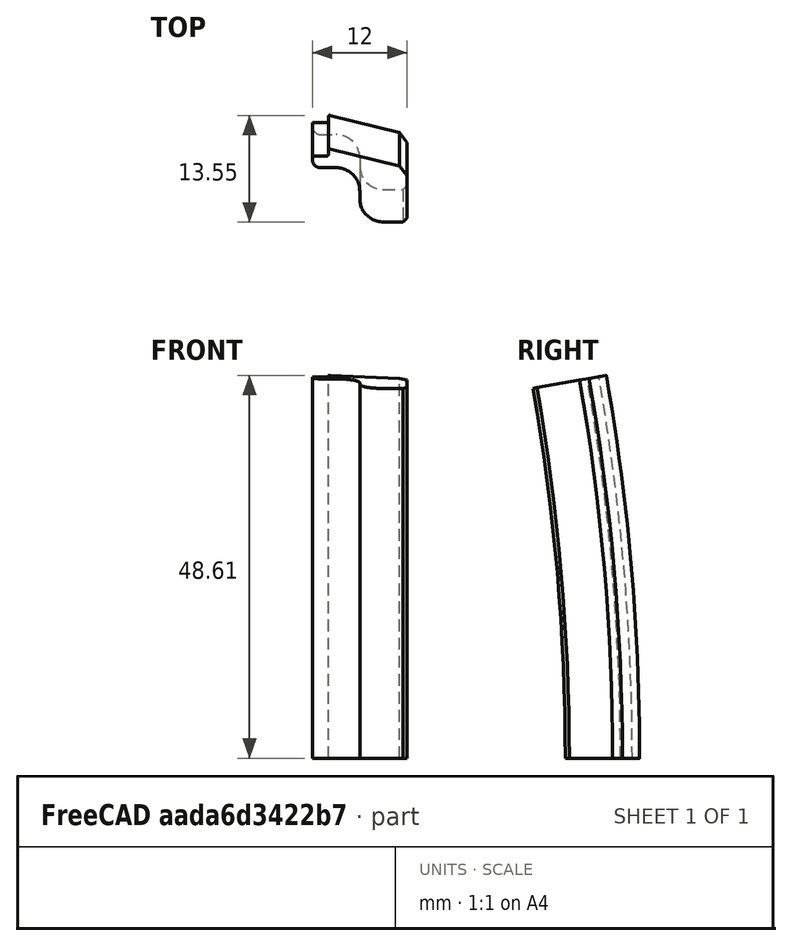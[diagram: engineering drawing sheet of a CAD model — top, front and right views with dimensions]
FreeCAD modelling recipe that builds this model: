
FCSTD DOCUMENT  (FreeCAD 0.16R)
Label: BeadBlock1
License: All rights reserved
LicenseURL: http://en.wikipedia.org/wiki/All_rights_reserved
objects: PartDesign::Fillet×5, PartDesign::Chamfer×2, Sketcher::SketchObject×1, PartDesign::Revolution×1, Mesh::Feature×1
note: 10 computed .brp shape members not serialized (recipe doc carries the construction recipe); baked Part::Feature solids carry a one-line shape summary decoded from their .brp

FEATURE [Sketcher::SketchObject] Sketch
  sketch-geometry (8):
    g0: LineSegment StartX=0 StartY=279 StartZ=0 EndX=2 EndY=279 EndZ=0
    g1: LineSegment StartX=2 StartY=279 StartZ=0 EndX=2 EndY=280 EndZ=0
    g2: LineSegment StartX=0 StartY=277.5 StartZ=0 EndX=0 EndY=279 EndZ=0
    g3: LineSegment StartX=0 StartY=277.5 StartZ=0 EndX=6 EndY=277.5 EndZ=0
    g4: LineSegment StartX=6 StartY=277.5 StartZ=0 EndX=6 EndY=270.5 EndZ=0
    g5: LineSegment StartX=6 StartY=270.5 StartZ=0 EndX=12 EndY=270.5 EndZ=0
    g6: LineSegment StartX=12 StartY=270.5 StartZ=0 EndX=12 EndY=277.5 EndZ=0
    g7: LineSegment StartX=2 StartY=280 StartZ=0 EndX=12 EndY=277.5 EndZ=0
  constraints (24):
    c: Horizontal(g0)
    c: PointOnObject(g0,g-2)
    c: DistanceY(g0) = 279
    c: Distance(g0) = 2
    c: Coincident(g1,g0)
    c: Vertical(g1)
    c: Distance(g1) = 1
    c: Vertical(g2)
    c: Coincident(g2,g0)
    c: Distance(g2) = 1.5
    c: Horizontal(g3)
    c: Coincident(g3,g2)
    c: Distance(g3) = 6
    c: Vertical(g4)
    c: Coincident(g4,g3)
    c: Distance(g4) = 7
    c: Horizontal(g5)
    c: Coincident(g5,g4)
    c: Distance(g5) = 6
    c: Vertical(g6)
    c: Coincident(g5,g6)
    c: Distance(g6) = 7
    c: Coincident(g7,g1)
    c: Coincident(g7,g6)
FEATURE [PartDesign::Revolution] Revolution
  Angle = 10
  Axis = (1,0,0)
  Base = (0,0,0)
  ReferenceAxis = -> Sketch [H_Axis]
  Sketch = -> Sketch
FEATURE [PartDesign::Fillet] Fillet
  Base = -> Revolution [Edge17]
  Radius = 3
FEATURE [PartDesign::Fillet] Fillet001
  Base = -> Fillet [Edge23]
  Radius = 1
FEATURE [PartDesign::Fillet] Fillet002
  Base = -> Fillet001 [Edge26]
  Radius = 0.2
FEATURE [PartDesign::Fillet] Fillet003
  Base = -> Fillet002 [Edge13]
  Radius = 0.2
FEATURE [PartDesign::Chamfer] Chamfer
  Base = -> Fillet003 [Edge22]
  Size = 1
FEATURE [PartDesign::Chamfer] Chamfer001
  Base = -> Chamfer [Edge21]
  Size = 0.5
FEATURE [PartDesign::Fillet] Fillet004
  Base = -> Chamfer001 [Edge22]
  Radius = 3
FEATURE [Mesh::Feature] Mesh  label="Fillet004 (Meshed)"
